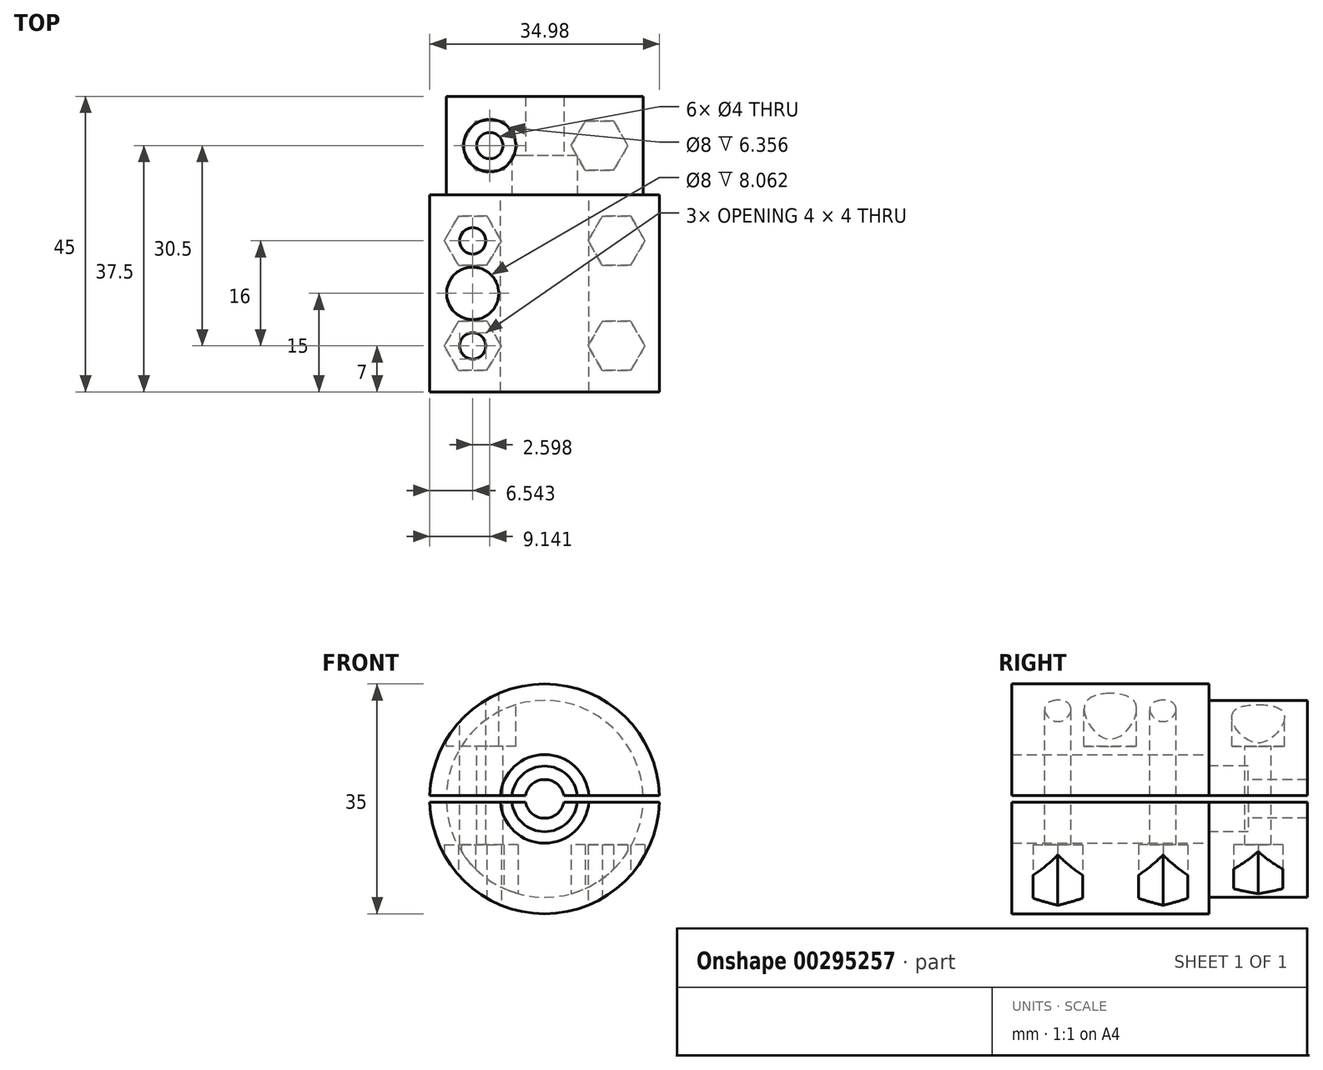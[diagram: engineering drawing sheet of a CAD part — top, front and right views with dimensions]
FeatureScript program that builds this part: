
annotation { "Feature Type Name" : "Feature", "Feature Type Description" : "" }
export const myFeature = defineFeature(function(context is Context, id is Id, definition is map)
    precondition{}
    {
        {
            var Q0;
            Q0=qCreatedBy(makeId("Front.planeOp"),FACE);
            var sketch = newSketch(context, id + "F0", { "sketchPlane" : qUnion([Q0])});
            skCircle(sketch, "E0", {"center": v(0, 0) * mm, "radius": 17.5 * mm});
            skCircle(sketch, "E1", {"center": v(0, 0) * mm, "radius": 6.75 * mm});
            skSolve(sketch);
        }
        {
            var Q0;
            Q0=makeQuery(id+"F0.imprint","IMPRINT",FACE,{"disambiguationData":[TD([[makeQuery(id+"F0.imprint","IMPRINT",EDGE,{"derivedFrom":sQuery(id+"F0.wireOp",EDGE,"E0")}),1.0]])]});
            extrude(context, id + "F1", {"entities" : qUnion([Q0]), "depth" : 30 * mm});
        }
        {
            var Q0;
            Q0=qCreatedBy(makeId("Front.planeOp"),FACE);
            var sketch = newSketch(context, id + "F2", { "sketchPlane" : qUnion([Q0])});
            skCircle(sketch, "E2", {"center": v(0, 0) * mm, "radius": 15 * mm});
            skCircle(sketch, "E3", {"center": v(0, 0) * mm, "radius": 2.95 * mm});
            skSolve(sketch);
        }
        {
            var Q0;
            Q0=makeQuery(id+"F2.imprint","IMPRINT",FACE,{"disambiguationData":[TD([[makeQuery(id+"F2.imprint","IMPRINT",EDGE,{"derivedFrom":sQuery(id+"F2.wireOp",EDGE,"E2")}),1.0]])]});
            extrude(context, id + "F3", {"entities" : qUnion([Q0]), "operationType" : NewBodyOperationType.ADD, "oppositeDirection" : true, "depth" : 15 * mm});
        }
        {
            var Q0;
            Q0=qCreatedBy(makeId("Right.planeOp"),FACE);
            var sketch = newSketch(context, id + "F4", { "sketchPlane" : qUnion([Q0])});
            skLineSegment(sketch, "E4.bottom", {"start": v(32.11, -0.5) * mm, "end": v(-50, -0.5) * mm});
            skLineSegment(sketch, "E4.top", {"start": v(32.11, 0.5) * mm, "end": v(-50, 0.5) * mm});
            skLineSegment(sketch, "E4.left", {"start": v(32.11, -0.5) * mm, "end": v(32.11, 0.5) * mm});
            skLineSegment(sketch, "E4.right", {"start": v(-50, -0.5) * mm, "end": v(-50, 0.5) * mm});
            skLineSegment(sketch, "E5", {"start": v(0, 22.27) * mm, "end": v(0, -11.94) * mm, "construction": true});
            skLineSegment(sketch, "E6", {"start": v(-18.65, 0) * mm, "end": v(24.46, 0) * mm, "construction": true});
            skSolve(sketch);
        }
        {
            var Q0;
            Q0=makeQuery(id+"F4.imprint","IMPRINT",FACE,{"disambiguationData":[TD([[makeQuery(id+"F4.imprint","IMPRINT",EDGE,{"derivedFrom":sQuery(id+"F4.wireOp",EDGE,"E4.bottom")}),-1.0]])]});
            extrude(context, id + "F5", {"entities" : qUnion([Q0]), "operationType" : NewBodyOperationType.REMOVE, "endBound" : BoundingType.SYMMETRIC, "depth" : 50 * mm});
        }
        {
            var Q0;
            Q0=qCreatedBy(makeId("Top.planeOp"),FACE);
            var sketch = newSketch(context, id + "F6", { "sketchPlane" : qUnion([Q0])});
            skCircle(sketch, "E7", {"center": v(-8.35, 7.5) * mm, "radius": 2 * mm});
            skLineSegment(sketch, "E8", {"start": v(-13.77, 7.5) * mm, "end": v(-4.22, 7.5) * mm, "construction": true});
            skLineSegment(sketch, "E9", {"start": v(-8.35, 10.05) * mm, "end": v(-8.35, 3.56) * mm, "construction": true});
            skLineSegment(sketch, "E10", {"start": v(-10.95, -2.34) * mm, "end": v(-10.95, -27.42) * mm, "construction": true});
            skCircle(sketch, "E11.MirrorC", {"center": v(8.35, 7.5) * mm, "radius": 2 * mm});
            skCircle(sketch, "E12", {"center": v(-10.95, -7) * mm, "radius": 2 * mm});
            skCircle(sketch, "E13", {"center": v(-10.95, -23) * mm, "radius": 2 * mm});
            skPoint(sketch, "E14.center.orphan", {"position": v(-10.95, -15) * mm});
            skPoint(sketch, "E15.MirrorC.center.orphan", {"position": v(10.95, -15) * mm});
            skCircle(sketch, "E16.MirrorC", {"center": v(10.95, -23) * mm, "radius": 2 * mm});
            skCircle(sketch, "E17.MirrorC", {"center": v(10.95, -7) * mm, "radius": 2 * mm});
            skSolve(sketch);
        }
        {
            var Q0;
            Q0=makeQuery(id+"F6.imprint","IMPRINT",FACE,{"disambiguationData":[TD([[makeQuery(id+"F6.imprint","IMPRINT",EDGE,{"derivedFrom":sQuery(id+"F6.wireOp",EDGE,"E7")}),1.0]])]});
            var Q1;
            Q1=makeQuery(id+"F6.imprint","IMPRINT",FACE,{"disambiguationData":[TD([[makeQuery(id+"F6.imprint","IMPRINT",EDGE,{"derivedFrom":sQuery(id+"F6.wireOp",EDGE,"E11.MirrorC")}),-1.0]])]});
            var Q2;
            Q2=makeQuery(id+"F6.imprint","IMPRINT",FACE,{"disambiguationData":[TD([[makeQuery(id+"F6.imprint","IMPRINT",EDGE,{"derivedFrom":sQuery(id+"F6.wireOp",EDGE,"E12")}),1.0]])]});
            var Q3;
            Q3=makeQuery(id+"F6.imprint","IMPRINT",FACE,{"disambiguationData":[TD([[makeQuery(id+"F6.imprint","IMPRINT",EDGE,{"derivedFrom":sQuery(id+"F6.wireOp",EDGE,"E13")}),1.0]])]});
            var Q4;
            Q4=makeQuery(id+"F6.imprint","IMPRINT",FACE,{"disambiguationData":[TD([[makeQuery(id+"F6.imprint","IMPRINT",EDGE,{"derivedFrom":sQuery(id+"F6.wireOp",EDGE,"E16.MirrorC")}),-1.0]])]});
            var Q5;
            Q5=makeQuery(id+"F6.imprint","IMPRINT",FACE,{"disambiguationData":[TD([[makeQuery(id+"F6.imprint","IMPRINT",EDGE,{"derivedFrom":sQuery(id+"F6.wireOp",EDGE,"E17.MirrorC")}),-1.0]])]});
            extrude(context, id + "F7", {"entities" : qUnion([Q0, Q1, Q2, Q3, Q4, Q5]), "operationType" : NewBodyOperationType.REMOVE, "endBound" : BoundingType.SYMMETRIC, "oppositeDirection" : true, "depth" : 40 * mm});
        }
        {
            var Q0;
            Q0=qCreatedBy(makeId("Top.planeOp"),FACE);
            cPlane(context, id + "F8", {"entities" : qUnion([Q0]), "cplaneType" : CPlaneType.OFFSET, "offset" : 20 * mm, "width" : 150 * mm, "height" : 150 * mm});
        }
        {
            var Q0;
            Q0=qCreatedBy(id+"F8.planeOp",FACE);
            var sketch = newSketch(context, id + "F9", { "sketchPlane" : qUnion([Q0])});
            skLineSegment(sketch, "E18", {"start": v(-14.29, -15) * mm, "end": v(-7.18, -15) * mm, "construction": true});
            skLineSegment(sketch, "E19", {"start": v(-10.95, -12.35) * mm, "end": v(-10.95, -19.31) * mm, "construction": true});
            skLineSegment(sketch, "E20", {"start": v(-8.35, 11.54) * mm, "end": v(-8.35, 3.76) * mm, "construction": true});
            skLineSegment(sketch, "E21", {"start": v(-5.47, 7.5) * mm, "end": v(-11.21, 7.5) * mm, "construction": true});
            skCircle(sketch, "E22", {"center": v(-10.95, -15) * mm, "radius": 4 * mm});
            skCircle(sketch, "E23", {"center": v(-8.35, 7.5) * mm, "radius": 4 * mm});
            skCircle(sketch, "E24.MirrorC", {"center": v(8.35, 7.5) * mm, "radius": 4 * mm});
            skCircle(sketch, "E25.MirrorC", {"center": v(10.95, -15) * mm, "radius": 4 * mm});
            skSolve(sketch);
        }
        {
            var Q0;
            Q0=makeQuery(id+"F9.imprint","IMPRINT",FACE,{"disambiguationData":[TD([[makeQuery(id+"F9.imprint","IMPRINT",EDGE,{"derivedFrom":sQuery(id+"F9.wireOp",EDGE,"E23")}),1.0]])]});
            var Q1;
            Q1=makeQuery(id+"F9.imprint","IMPRINT",FACE,{"disambiguationData":[TD([[makeQuery(id+"F9.imprint","IMPRINT",EDGE,{"derivedFrom":sQuery(id+"F9.wireOp",EDGE,"E24.MirrorC")}),-1.0]])]});
            var Q2;
            Q2=makeQuery(id+"F9.imprint","IMPRINT",FACE,{"disambiguationData":[TD([[makeQuery(id+"F9.imprint","IMPRINT",EDGE,{"derivedFrom":sQuery(id+"F9.wireOp",EDGE,"E25.MirrorC")}),-1.0]])]});
            var Q3;
            Q3=makeQuery(id+"F9.imprint","IMPRINT",FACE,{"disambiguationData":[TD([[makeQuery(id+"F9.imprint","IMPRINT",EDGE,{"derivedFrom":sQuery(id+"F9.wireOp",EDGE,"E22")}),1.0]])]});
            extrude(context, id + "F10", {"entities" : qUnion([Q0, Q1, Q2, Q3]), "operationType" : NewBodyOperationType.REMOVE, "oppositeDirection" : true, "depth" : 12 * mm});
        }
        {
            var Q0;
            Q0=qCreatedBy(makeId("Top.planeOp"),FACE);
            cPlane(context, id + "F11", {"entities" : qUnion([Q0]), "cplaneType" : CPlaneType.OFFSET, "offset" : 20 * mm, "oppositeDirection" : true, "width" : 150 * mm, "height" : 150 * mm});
        }
        {
            var Q0;
            Q0=qCreatedBy(id+"F11.planeOp",FACE);
            var sketch = newSketch(context, id + "F12", { "sketchPlane" : qUnion([Q0])});
            skLineSegment(sketch, "E26", {"start": v(10.95, -16.04) * mm, "end": v(10.95, -13.62) * mm, "construction": true});
            skPoint(sketch, "E27.0.midPoint", {"position": v(10.95, -22.16) * mm});
            skLineSegment(sketch, "E28", {"start": v(8.35, 8.5) * mm, "end": v(8.35, 6.53) * mm, "construction": true});
            skLineSegment(sketch, "E29", {"start": v(6.87, 7.5) * mm, "end": v(9.82, 7.5) * mm, "construction": true});
            skCircle(sketch, "E30.cCircle", {"center": v(8.35, 7.5) * mm, "radius": 3.75 * mm, "construction": true});
            skLineSegment(sketch, "E30.0", {"start": v(6.18, 3.75) * mm, "end": v(4.02, 7.5) * mm});
            skLineSegment(sketch, "E30.1", {"start": v(4.02, 7.5) * mm, "end": v(6.18, 11.25) * mm});
            skLineSegment(sketch, "E30.2", {"start": v(6.18, 11.25) * mm, "end": v(10.51, 11.25) * mm});
            skLineSegment(sketch, "E30.3", {"start": v(10.51, 11.25) * mm, "end": v(12.68, 7.5) * mm});
            skLineSegment(sketch, "E30.4", {"start": v(12.68, 7.5) * mm, "end": v(10.51, 3.75) * mm});
            skLineSegment(sketch, "E30.5", {"start": v(10.51, 3.75) * mm, "end": v(6.18, 3.75) * mm});
            skPoint(sketch, "E30.0.midPoint", {"position": v(5.1, 5.63) * mm});
            skLineSegment(sketch, "E31.MirrorCS", {"start": v(-10.51, 3.75) * mm, "end": v(-6.18, 3.75) * mm});
            skLineSegment(sketch, "E32.MirrorCS", {"start": v(-6.18, 3.75) * mm, "end": v(-4.02, 7.5) * mm});
            skLineSegment(sketch, "E33.MirrorCS", {"start": v(-12.68, 7.5) * mm, "end": v(-10.51, 3.75) * mm});
            skLineSegment(sketch, "E34.MirrorCS", {"start": v(-10.51, 11.25) * mm, "end": v(-12.68, 7.5) * mm});
            skLineSegment(sketch, "E35.MirrorCS", {"start": v(-6.18, 11.25) * mm, "end": v(-10.51, 11.25) * mm});
            skLineSegment(sketch, "E36.MirrorCS", {"start": v(-4.02, 7.5) * mm, "end": v(-6.18, 11.25) * mm});
            skLineSegment(sketch, "E37", {"start": v(10.95, -29) * mm, "end": v(10.95, -7) * mm, "construction": true});
            skCircle(sketch, "E38.cCircle", {"center": v(10.95, -6.98) * mm, "radius": 3.75 * mm, "construction": true});
            skLineSegment(sketch, "E38.0", {"start": v(8.78, -3.23) * mm, "end": v(13.11, -3.23) * mm});
            skLineSegment(sketch, "E38.1", {"start": v(13.11, -3.23) * mm, "end": v(15.28, -6.98) * mm});
            skLineSegment(sketch, "E38.2", {"start": v(15.28, -6.98) * mm, "end": v(13.11, -10.73) * mm});
            skLineSegment(sketch, "E38.3", {"start": v(13.11, -10.73) * mm, "end": v(8.78, -10.73) * mm});
            skLineSegment(sketch, "E38.4", {"start": v(8.78, -10.73) * mm, "end": v(6.62, -6.98) * mm});
            skLineSegment(sketch, "E38.5", {"start": v(6.62, -6.98) * mm, "end": v(8.78, -3.23) * mm});
            skPoint(sketch, "E38.0.midPoint", {"position": v(10.95, -3.23) * mm});
            skCircle(sketch, "E39.cCircle", {"center": v(10.95, -23) * mm, "radius": 3.75 * mm, "construction": true});
            skLineSegment(sketch, "E39.0", {"start": v(13.11, -26.75) * mm, "end": v(8.78, -26.75) * mm});
            skLineSegment(sketch, "E39.1", {"start": v(8.78, -26.75) * mm, "end": v(6.62, -23) * mm});
            skLineSegment(sketch, "E39.2", {"start": v(6.62, -23) * mm, "end": v(8.78, -19.25) * mm});
            skLineSegment(sketch, "E39.3", {"start": v(8.78, -19.25) * mm, "end": v(13.11, -19.25) * mm});
            skLineSegment(sketch, "E39.4", {"start": v(13.11, -19.25) * mm, "end": v(15.28, -23) * mm});
            skLineSegment(sketch, "E39.5", {"start": v(15.28, -23) * mm, "end": v(13.11, -26.75) * mm});
            skPoint(sketch, "E39.0.midPoint", {"position": v(10.95, -26.75) * mm});
            skLineSegment(sketch, "E40.MirrorCS", {"start": v(-8.78, -26.75) * mm, "end": v(-6.62, -23) * mm});
            skLineSegment(sketch, "E41.MirrorCS", {"start": v(-13.11, -26.75) * mm, "end": v(-8.78, -26.75) * mm});
            skLineSegment(sketch, "E42.MirrorCS", {"start": v(-15.28, -23) * mm, "end": v(-13.11, -26.75) * mm});
            skLineSegment(sketch, "E43.MirrorCS", {"start": v(-13.11, -19.25) * mm, "end": v(-15.28, -23) * mm});
            skLineSegment(sketch, "E44.MirrorCS", {"start": v(-8.78, -19.25) * mm, "end": v(-13.11, -19.25) * mm});
            skLineSegment(sketch, "E45.MirrorCS", {"start": v(-6.62, -23) * mm, "end": v(-8.78, -19.25) * mm});
            skLineSegment(sketch, "E46.MirrorCS", {"start": v(-13.11, -10.73) * mm, "end": v(-8.78, -10.73) * mm});
            skLineSegment(sketch, "E47.MirrorCS", {"start": v(-8.78, -10.73) * mm, "end": v(-6.62, -6.98) * mm});
            skLineSegment(sketch, "E48.MirrorCS", {"start": v(-6.62, -6.98) * mm, "end": v(-8.78, -3.23) * mm});
            skLineSegment(sketch, "E49.MirrorCS", {"start": v(-15.28, -6.98) * mm, "end": v(-13.11, -10.73) * mm});
            skLineSegment(sketch, "E50.MirrorCS", {"start": v(-13.11, -3.23) * mm, "end": v(-15.28, -6.98) * mm});
            skLineSegment(sketch, "E51.MirrorCS", {"start": v(-8.78, -3.23) * mm, "end": v(-13.11, -3.23) * mm});
            skSolve(sketch);
        }
        {
            var Q0;
            Q0=makeQuery(id+"F12.imprint","IMPRINT",FACE,{"disambiguationData":[TD([[makeQuery(id+"F12.imprint","IMPRINT",EDGE,{"derivedFrom":sQuery(id+"F12.wireOp",EDGE,"E40.MirrorCS")}),1.0]])]});
            var Q1;
            Q1=makeQuery(id+"F12.imprint","IMPRINT",FACE,{"disambiguationData":[TD([[makeQuery(id+"F12.imprint","IMPRINT",EDGE,{"derivedFrom":sQuery(id+"F12.wireOp",EDGE,"E39.0")}),-1.0]])]});
            var Q2;
            Q2=makeQuery(id+"F12.imprint","IMPRINT",FACE,{"disambiguationData":[TD([[makeQuery(id+"F12.imprint","IMPRINT",EDGE,{"derivedFrom":sQuery(id+"F12.wireOp",EDGE,"E38.0")}),-1.0]])]});
            var Q3;
            Q3=makeQuery(id+"F12.imprint","IMPRINT",FACE,{"disambiguationData":[TD([[makeQuery(id+"F12.imprint","IMPRINT",EDGE,{"derivedFrom":sQuery(id+"F12.wireOp",EDGE,"E46.MirrorCS")}),1.0]])]});
            var Q4;
            Q4=makeQuery(id+"F12.imprint","IMPRINT",FACE,{"disambiguationData":[TD([[makeQuery(id+"F12.imprint","IMPRINT",EDGE,{"derivedFrom":sQuery(id+"F12.wireOp",EDGE,"E31.MirrorCS")}),1.0]])]});
            var Q5;
            Q5=makeQuery(id+"F12.imprint","IMPRINT",FACE,{"disambiguationData":[TD([[makeQuery(id+"F12.imprint","IMPRINT",EDGE,{"derivedFrom":sQuery(id+"F12.wireOp",EDGE,"E30.0")}),-1.0]])]});
            extrude(context, id + "F13", {"entities" : qUnion([Q0, Q1, Q2, Q3, Q4, Q5]), "operationType" : NewBodyOperationType.REMOVE, "depth" : 13 * mm});
        }
        {
            var Q0;
            {var subQ0=sQuery(id+"F2.wireOp",EDGE,"E3");Q0=makeQuery(id+"F5.boolean.opBoolean","SPLIT",FACE,{"disambiguationData":[TD([makeQuery(id+"F5.opExtrude","SWEPT_FACE",FACE,{"disambiguationData":[OSD([sQuery(id+"F4.wireOp",EDGE,"E4.top")])]})])],"derivedFrom":makeQuery(id+"F3.opExtrude","CAP_FACE",FACE,{"disambiguationData":[OSD([sQuery(id+"F2.wireOp",EDGE,"E2"),subQ0])],"isStart":true})});}
            var sketch = newSketch(context, id + "F14", { "sketchPlane" : qUnion([Q0])});
            skCircle(sketch, "E52", {"center": v(0, 0) * mm, "radius": 5 * mm});
            skSolve(sketch);
        }
        {
            var Q0;
            {var subQ1=makeQuery(id+"F5.opExtrude","SWEPT_FACE",FACE,{"disambiguationData":[OSD([sQuery(id+"F4.wireOp",EDGE,"E4.top")])]});var subQ2=sQuery(id+"F2.wireOp",EDGE,"E3");var subQ9=makeQuery(id+"F5.boolean.opBoolean","SPLIT",EDGE,{"disambiguationData":[TD([subQ1])],"derivedFrom":makeQuery(id+"F3.opExtrude","CAP_EDGE",EDGE,{"disambiguationData":[OSD([subQ2])],"isStart":true})});Q0=makeQuery(id+"F14.imprint","IMPRINT",FACE,{"disambiguationData":[TD([[makeQuery(id+"F14.imprint","IMPRINT",EDGE,{"derivedFrom":subQ9}),-1.0]])]});}
            var Q1;
            {var subQ1=makeQuery(id+"F5.opExtrude","SWEPT_FACE",FACE,{"disambiguationData":[OSD([sQuery(id+"F4.wireOp",EDGE,"E4.top")])]});var subQ2=sQuery(id+"F2.wireOp",EDGE,"E3");var subQ9=makeQuery(id+"F5.boolean.opBoolean","SPLIT",EDGE,{"disambiguationData":[TD([subQ1])],"derivedFrom":makeQuery(id+"F3.opExtrude","CAP_EDGE",EDGE,{"disambiguationData":[OSD([subQ2])],"isStart":true})});Q1=makeQuery(id+"F14.imprint","IMPRINT",FACE,{"disambiguationData":[TD([[makeQuery(id+"F14.imprint","IMPRINT",EDGE,{"derivedFrom":subQ9}),1.0]])]});}
            extrude(context, id + "F15", {"entities" : qUnion([Q0, Q1]), "operationType" : NewBodyOperationType.REMOVE, "oppositeDirection" : true, "depth" : 6 * mm});
        }
    });
